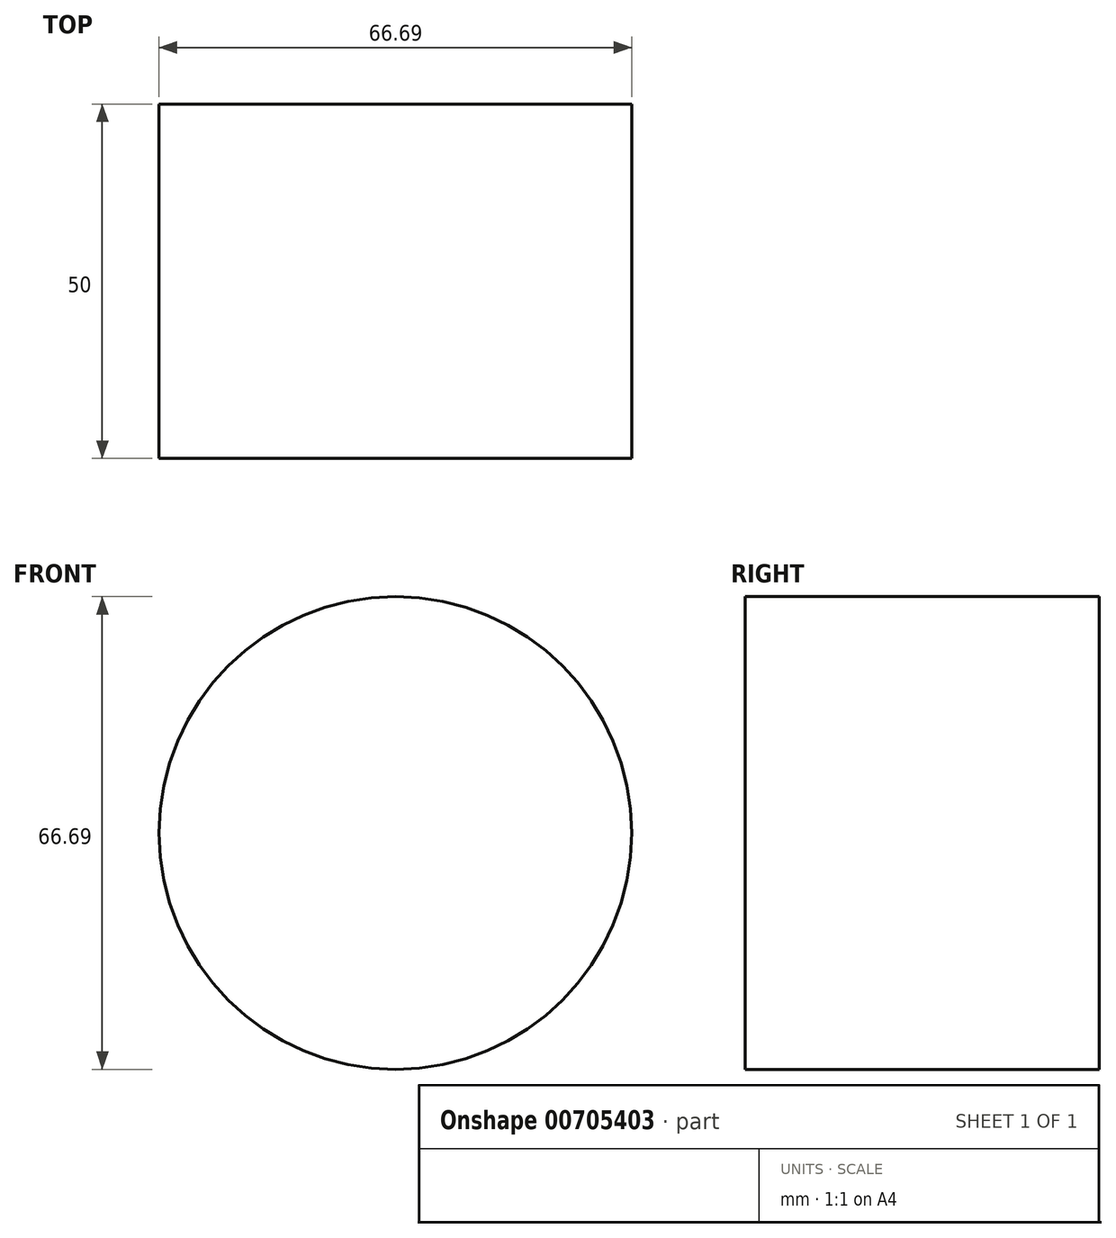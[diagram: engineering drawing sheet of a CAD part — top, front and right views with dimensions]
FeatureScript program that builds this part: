
annotation { "Feature Type Name" : "Feature", "Feature Type Description" : "" }
export const myFeature = defineFeature(function(context is Context, id is Id, definition is map)
    precondition{}
    {
        {
            var Q0;
            Q0=qCreatedBy(makeId("Front.planeOp"),FACE);
            var sketch = newSketch(context, id + "F0", { "sketchPlane" : qUnion([Q0])});
            skCircle(sketch, "E0", {"center": v(-29.32, 27.89) * mm, "radius": 33.34 * mm});
            skSolve(sketch);
        }
        {
            var Q0;
            Q0=makeQuery(id+"F0.imprint","IMPRINT",FACE,{"disambiguationData":[TD([[makeQuery(id+"F0.imprint","IMPRINT",EDGE,{"derivedFrom":sQuery(id+"F0.wireOp",EDGE,"E0")}),1.0]])]});
            extrude(context, id + "F1", {"entities" : qUnion([Q0]), "depth" : 50 * mm, "offsetDistance" : 25 * mm});
        }
        {
            var Q0;
            Q0=makeQuery(id+"F1.opExtrude","CAP_FACE",FACE,{"disambiguationData":[OSD([sQuery(id+"F0.wireOp",EDGE,"E0")])],"isStart":true});
            var sketch = newSketch(context, id + "F2", { "sketchPlane" : qUnion([Q0])});
            skCircle(sketch, "E1", {"center": v(29.32, 27.89) * mm, "radius": 20.18 * mm});
            skSolve(sketch);
        }
        {
            var Q0;
            Q0=sQuery(id+"F2.wireOp",EDGE,"E1");
            extrude(context, id + "F3", {"bodyType" : ToolBodyType.SURFACE, "surfaceEntities" : qUnion([Q0]), "oppositeDirection" : true, "depth" : 50 * mm, "offsetDistance" : 25 * mm, "hasDraft" : true, "draftAngle" : 3 * degree, "hasSecondDirection" : true, "secondDirectionOppositeDirection" : true, "secondDirectionDepth" : 25 * mm});
        }
    });
